# Revit family: 3097177 Lighting Fixture_Sylvania_Insaver LED 75 - Round - White Bezel_Ceiling Recessed
name_source: partatom
category: Lighting Fixtures
revit_build: Autodesk Revit 2017 (Build: 20190507_1515(x64)
units: mm (PartAtom-declared; Revit-internal decimal feet)

## family parameters
Cut with Voids When Loaded = No
Host = Face
Light Source = Yes
OmniClass Number = 23.80.70.11.17
OmniClass Title = Specialized Lighting by Location or Use
Part Type = Normal
Room Calculation Point = No
Round Connector Dimension = Use Diameter
Shared = No

## types (2) — shared parameters
Accesory Material = Metallic Paint_Sylvania_Insaver LED 75_White_RAL 9016
Apparent Load = 16 VA
Assembly Code = D5020200
Beam Angle = 55°
CRI ( Ra ) = 85
Color Filter = 16777215
Cutout Diameter = 75 mm
Description = Innovative square or round design using array chip technology High colour
rendering index CRI Thermal management ensures service life up to 50.000
hrs Low power consumption - 16W
Diameter = 90 mm  [stored 0.295276 ft]
Dimming Lamp Color Temperature Shift = <None>
Drive Current = 350 mA
Electrical Protection = Class II
Emit Shape Visible in Rendering = No
Emit from Circle Diameter = 50 mm
Height = 65 mm  [stored 0.213255 ft]
IP Rating = IP65
Lamp = 16W High Brightnes LED array
Lamp Comments = Integrated LED
Life = 50 000 h
Manufacturer = Feilo Sylvania
Product Family = Insaver LED 75 - Round - White Bezel
Product Page URL = http://www.sylvania-lighting.com
Radius = 45 mm  [stored 0.147638 ft]
Reflector Material = Aluminium_Sylvania_Insaver LED 75_Silver
T Class Max = -1 °C
T Class Min = -1 °C
Tilt Angle = -90°
Transformator Marerial = Metallic Paint_Sylvania_Insaver LED 75_Black_RAL 9005
URL = http://www.sylvania-lighting.com
Voltage = 230 V
Voltage Comments = UNV (Universal Voltage; 230/240 Volt)
Weight = 0 kg
zero-valued in all types: Default Elevation

## per-type parameters (varying)
| type | Catalog Number | Photometric Web File |
| Insaver 75 LED RS 16W WW EB WH | 3097176 Insaver 75 LED RS 16W WW EB WH | 3097176_InsaverLED7513WWWSTD-98563.ies |
| Insaver 75 LED RD HO 16W NW EB WH | 3097177 Insaver 75 LED RD HO 16W NW EB WH | 3097177_Insaver75LEDRDHO16WNWEBWH-98583.ies |

note: column(s) folded — value = type name in every type: Model

note: [stored X ft] marks values corroborated as IEEE doubles in the binary element streams (Revit-internal decimal feet)

## geometry (parser evidence)
native form markers: Blend x4, Sweep x1
no freeform markers — native parametric forms only
